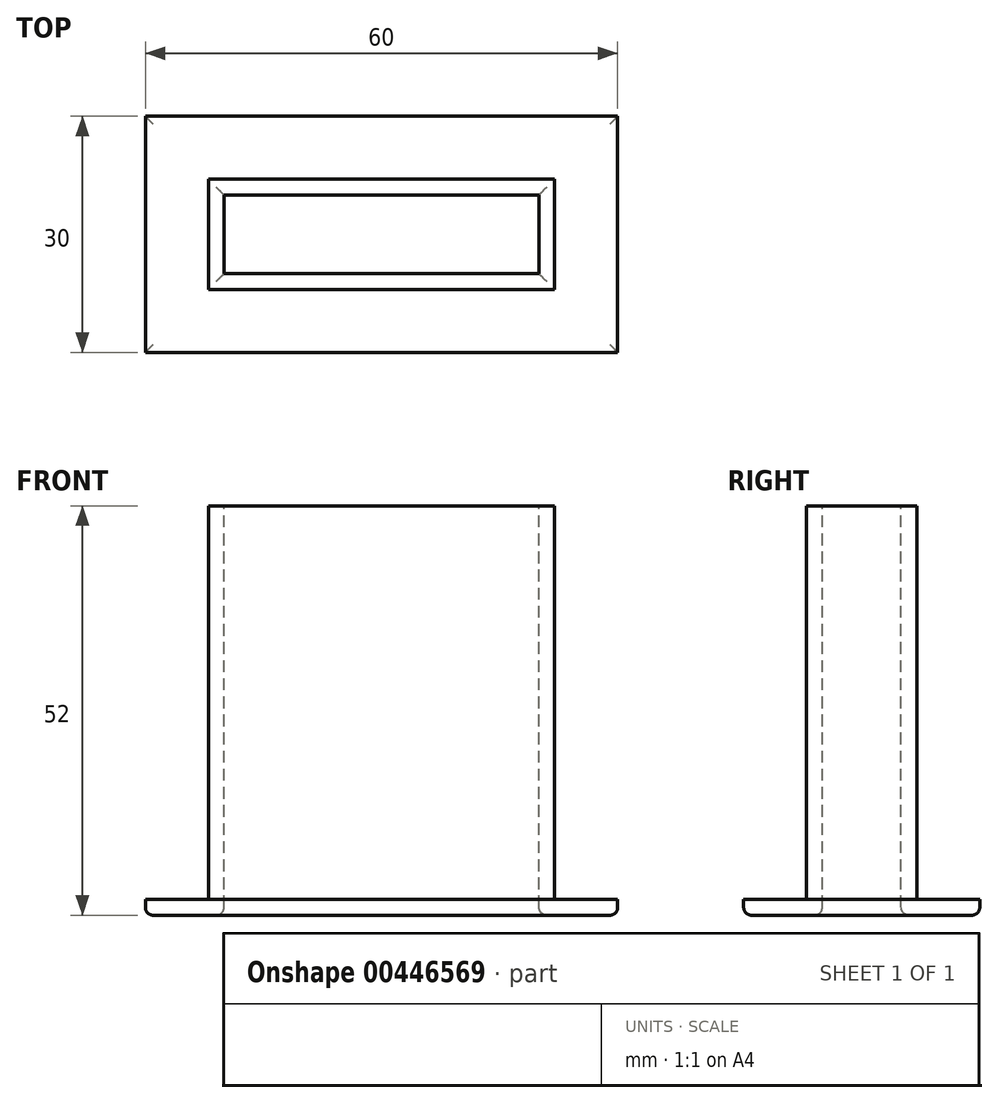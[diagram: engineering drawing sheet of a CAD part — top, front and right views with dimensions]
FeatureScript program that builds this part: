
annotation { "Feature Type Name" : "Feature", "Feature Type Description" : "" }
export const myFeature = defineFeature(function(context is Context, id is Id, definition is map)
    precondition{}
    {
        {
            var Q0;
            Q0=qCreatedBy(makeId("Top.planeOp"),FACE);
            var sketch = newSketch(context, id + "F0", { "sketchPlane" : qUnion([Q0])});
            skLineSegment(sketch, "E0.bottom", {"start": v(30, 15) * mm, "end": v(-30, 15) * mm});
            skLineSegment(sketch, "E0.top", {"start": v(30, -15) * mm, "end": v(-30, -15) * mm});
            skLineSegment(sketch, "E0.left", {"start": v(30, 15) * mm, "end": v(30, -15) * mm});
            skLineSegment(sketch, "E0.right", {"start": v(-30, 15) * mm, "end": v(-30, -15) * mm});
            skPoint(sketch, "E0.middle", {"position": v(0, 0) * mm});
            skSolve(sketch);
        }
        {
            var Q0;
            Q0=makeQuery(id+"F0.imprint","IMPRINT",FACE,{"disambiguationData":[TD([[makeQuery(id+"F0.imprint","IMPRINT",EDGE,{"derivedFrom":sQuery(id+"F0.wireOp",EDGE,"E0.bottom")}),1.0]])]});
            extrude(context, id + "F1", {"entities" : qUnion([Q0]), "depth" : 2 * mm});
        }
        {
            var Q0;
            Q0=makeQuery(id+"F1.opExtrude","CAP_FACE",FACE,{"disambiguationData":[OSD([sQuery(id+"F0.wireOp",EDGE,"E0.bottom"),sQuery(id+"F0.wireOp",EDGE,"E0.top"),sQuery(id+"F0.wireOp",EDGE,"E0.left"),sQuery(id+"F0.wireOp",EDGE,"E0.right")])],"isStart":false});
            var sketch = newSketch(context, id + "F2", { "sketchPlane" : qUnion([Q0])});
            skLineSegment(sketch, "E1.bottom", {"start": v(22, 7) * mm, "end": v(-22, 7) * mm});
            skLineSegment(sketch, "E1.top", {"start": v(22, -7) * mm, "end": v(-22, -7) * mm});
            skLineSegment(sketch, "E1.left", {"start": v(22, 7) * mm, "end": v(22, -7) * mm});
            skLineSegment(sketch, "E1.right", {"start": v(-22, 7) * mm, "end": v(-22, -7) * mm});
            skPoint(sketch, "E1.middle", {"position": v(0, 0) * mm});
            skSolve(sketch);
        }
        {
            var Q0;
            Q0=makeQuery(id+"F2.imprint","IMPRINT",FACE,{"disambiguationData":[TD([[makeQuery(id+"F2.imprint","IMPRINT",EDGE,{"derivedFrom":sQuery(id+"F2.wireOp",EDGE,"E1.bottom")}),1.0]])]});
            extrude(context, id + "F3", {"entities" : qUnion([Q0]), "operationType" : NewBodyOperationType.ADD, "depth" : 50 * mm});
        }
        {
            var Q0;
            Q0=makeQuery(id+"F3.opExtrude","CAP_FACE",FACE,{"disambiguationData":[OSD([sQuery(id+"F2.wireOp",EDGE,"E1.bottom"),sQuery(id+"F2.wireOp",EDGE,"E1.top"),sQuery(id+"F2.wireOp",EDGE,"E1.left"),sQuery(id+"F2.wireOp",EDGE,"E1.right")])],"isStart":false});
            var sketch = newSketch(context, id + "F4", { "sketchPlane" : qUnion([Q0])});
            skLineSegment(sketch, "E2.bottom", {"start": v(20, 5) * mm, "end": v(-20, 5) * mm});
            skLineSegment(sketch, "E2.top", {"start": v(20, -5) * mm, "end": v(-20, -5) * mm});
            skLineSegment(sketch, "E2.left", {"start": v(20, 5) * mm, "end": v(20, -5) * mm});
            skLineSegment(sketch, "E2.right", {"start": v(-20, 5) * mm, "end": v(-20, -5) * mm});
            skPoint(sketch, "E2.middle", {"position": v(0, 0) * mm});
            skSolve(sketch);
        }
        {
            var Q0;
            Q0=makeQuery(id+"F4.imprint","IMPRINT",FACE,{"disambiguationData":[TD([[makeQuery(id+"F4.imprint","IMPRINT",EDGE,{"derivedFrom":sQuery(id+"F4.wireOp",EDGE,"E2.bottom")}),1.0]])]});
            extrude(context, id + "F5", {"entities" : qUnion([Q0]), "operationType" : NewBodyOperationType.REMOVE, "endBound" : BoundingType.THROUGH_ALL, "oppositeDirection" : true, "depth" : 25 * mm});
        }
        {
            var Q0;
            Q0=makeQuery(id+"F1.opExtrude","CAP_FACE",FACE,{"disambiguationData":[OSD([sQuery(id+"F0.wireOp",EDGE,"E0.bottom"),sQuery(id+"F0.wireOp",EDGE,"E0.top"),sQuery(id+"F0.wireOp",EDGE,"E0.left"),sQuery(id+"F0.wireOp",EDGE,"E0.right")])],"isStart":true});
            var Q1;
            Q1=makeQuery(id+"F5.boolean.opBoolean","COPY",EDGE,{"derivedFrom":makeQuery(id+"F5.opExtrude","CAP_EDGE",EDGE,{"disambiguationData":[OSD([sQuery(id+"F4.wireOp",EDGE,"E2.bottom")])],"isStart":true})});
            var Q2;
            Q2=makeQuery(id+"F5.boolean.opBoolean","COPY",EDGE,{"derivedFrom":makeQuery(id+"F5.opExtrude","CAP_EDGE",EDGE,{"disambiguationData":[OSD([sQuery(id+"F4.wireOp",EDGE,"E2.right")])],"isStart":true})});
            var Q3;
            Q3=makeQuery(id+"F5.boolean.opBoolean","COPY",EDGE,{"derivedFrom":makeQuery(id+"F5.opExtrude","CAP_EDGE",EDGE,{"disambiguationData":[OSD([sQuery(id+"F4.wireOp",EDGE,"E2.top")])],"isStart":true})});
            var Q4;
            Q4=makeQuery(id+"F5.boolean.opBoolean","COPY",EDGE,{"derivedFrom":makeQuery(id+"F5.opExtrude","CAP_EDGE",EDGE,{"disambiguationData":[OSD([sQuery(id+"F4.wireOp",EDGE,"E2.left")])],"isStart":true})});
            fillet(context, id + "F6", {"entities" : qUnion([Q0, Q1, Q2, Q3, Q4]), "radius" : 1 * mm, "tangentPropagation" : true, "allowEdgeOverflow" : false});
        }
    });
